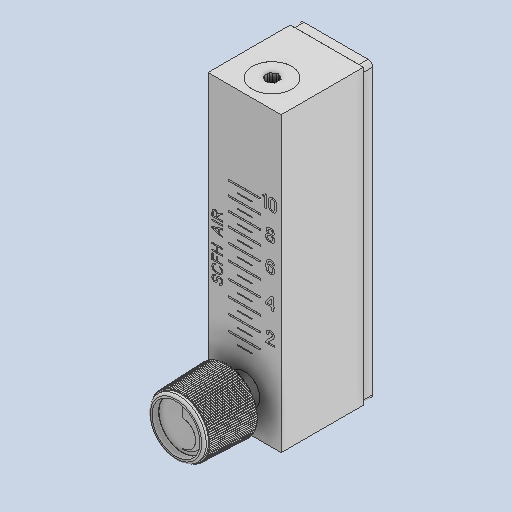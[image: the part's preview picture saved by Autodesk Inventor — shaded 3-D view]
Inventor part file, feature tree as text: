
AUTODESK INVENTOR PART (.ipt)
format: ipt  version: 2025 (Build 290162000, 162)  size: 10,302,976 bytes
history: native  units: mm
features: other x10, revolve x5, pattern_circular x1, mirror x1
ambient origin geometry x8: Origin, YZ Plane, XZ Plane, XY Plane, X Axis, Y Axis, Z Axis, Center Point
bodies: Solid1 (feature_tree), Solid2 (feature_tree), Solid3 (feature_tree), Solid4 (feature_tree), Solid5 (feature_tree), Solid6 (feature_tree), Solid7 (feature_tree), Solid8 (feature_tree), Solid9 (feature_tree), Solid10 (feature_tree), Solid11 (feature_tree), Solid12 (feature_tree), Solid13 (feature_tree), Solid14 (feature_tree), Solid15 (feature_tree), Solid16 (feature_tree), Solid17 (feature_tree)
feature tree (17):
  other  "Cut-Extrude2"
  other  "LPattern1"
  other  "Cut-Extrude4"
  other  "Cut-Extrude5"
  other  "Boss-Extrude3"
  revolve  "Revolve6"  [1 undecoded]
  revolve  "Revolve7"  [1 undecoded]
  pattern_circular  "CirPattern1"
  mirror  "Mirror1"
  other  "LPattern6"
  other  "Cut-Extrude13"
  other  "Boss-Extrude6"
  other  "Boss-Extrude7"
  revolve  "Revolve8"  [1 undecoded]
  other  "LPattern7"
  revolve  "Revolve9"  [1 undecoded]
  revolve  "Revolve10"  [1 undecoded]
note: 5 required parameter values undecoded (feature->parameter linkage not recoverable at this tier; creation-order binding heuristic only, values carry confidence <= 0.55)
